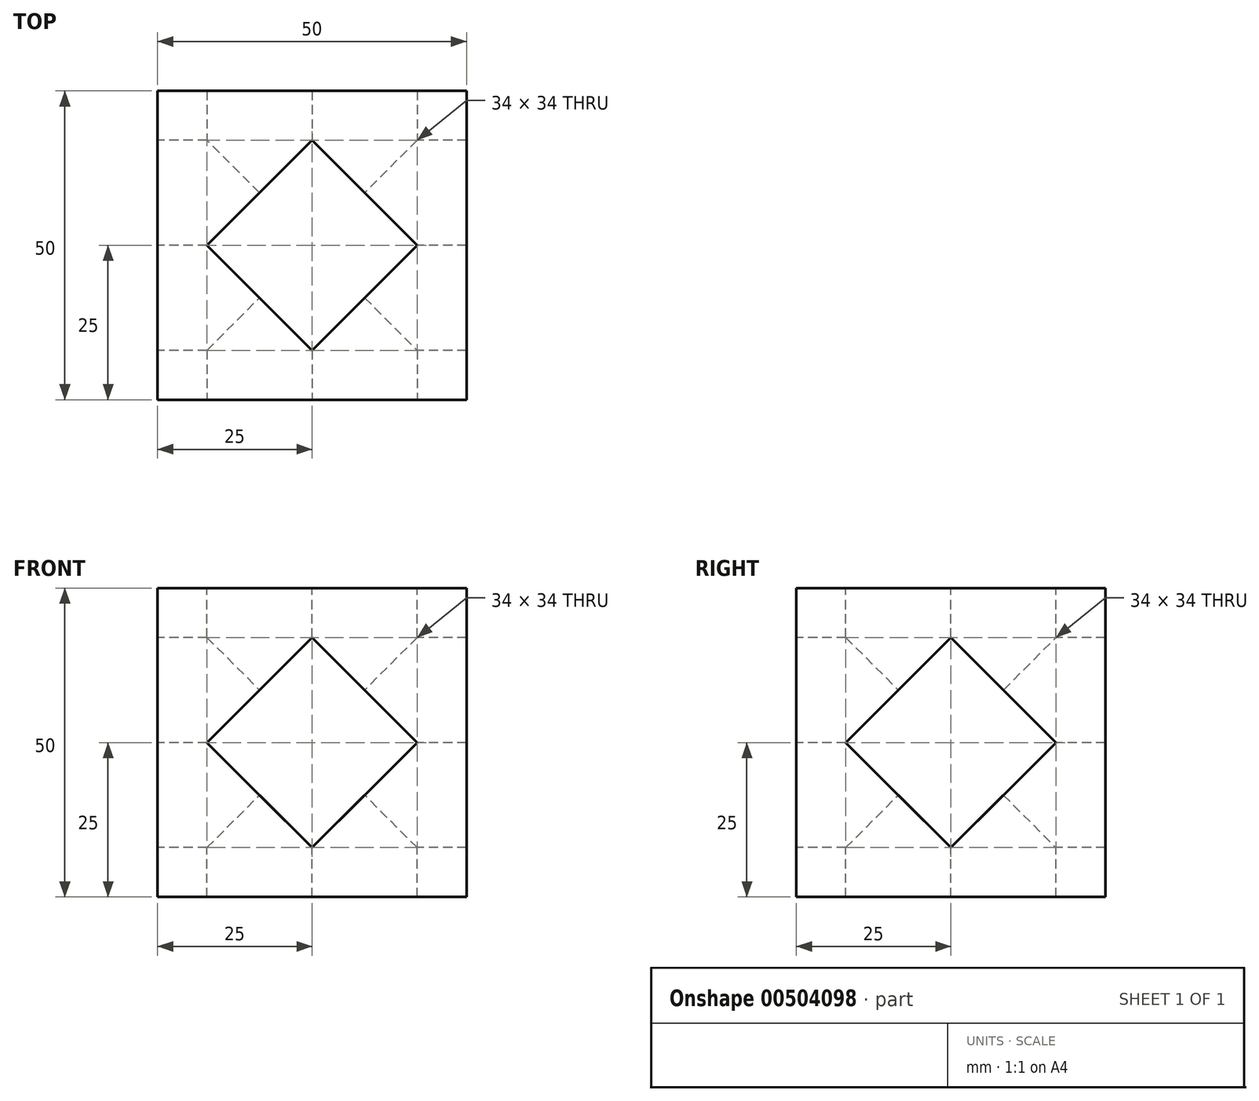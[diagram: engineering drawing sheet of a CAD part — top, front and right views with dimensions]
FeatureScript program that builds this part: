
annotation { "Feature Type Name" : "Feature", "Feature Type Description" : "" }
export const myFeature = defineFeature(function(context is Context, id is Id, definition is map)
    precondition{}
    {
        {
            var Q0;
            Q0=qCreatedBy(makeId("Top.planeOp"),FACE);
            var sketch = newSketch(context, id + "F0", { "sketchPlane" : qUnion([Q0])});
            skLineSegment(sketch, "E0.bottom", {"start": v(-25, -25) * mm, "end": v(25, -25) * mm});
            skLineSegment(sketch, "E0.top", {"start": v(-25, 25) * mm, "end": v(25, 25) * mm});
            skLineSegment(sketch, "E0.left", {"start": v(-25, -25) * mm, "end": v(-25, 25) * mm});
            skLineSegment(sketch, "E0.right", {"start": v(25, -25) * mm, "end": v(25, 25) * mm});
            skSolve(sketch);
        }
        {
            var Q0;
            Q0=makeQuery(id+"F0.imprint","IMPRINT",FACE,{"disambiguationData":[TD([[makeQuery(id+"F0.imprint","IMPRINT",EDGE,{"derivedFrom":sQuery(id+"F0.wireOp",EDGE,"E0.bottom")}),1.0]])]});
            extrude(context, id + "F1", {"entities" : qUnion([Q0]), "depth" : 50 * mm});
        }
        {
            var Q0;
            Q0=makeQuery(id+"F1.opExtrude","SWEPT_FACE",FACE,{"disambiguationData":[OSD([sQuery(id+"F0.wireOp",EDGE,"E0.bottom")])]});
            var sketch = newSketch(context, id + "F2", { "sketchPlane" : qUnion([Q0])});
            skLineSegment(sketch, "E1", {"start": v(0, 42) * mm, "end": v(17, 25) * mm});
            skLineSegment(sketch, "E2", {"start": v(17, 25) * mm, "end": v(0, 8) * mm});
            skLineSegment(sketch, "E3", {"start": v(0, 8) * mm, "end": v(-17, 25) * mm});
            skLineSegment(sketch, "E4", {"start": v(-17, 25) * mm, "end": v(0, 42) * mm});
            skSolve(sketch);
        }
        {
            var Q0;
            Q0=makeQuery(id+"F2.imprint","IMPRINT",FACE,{"disambiguationData":[TD([[makeQuery(id+"F2.imprint","IMPRINT",EDGE,{"derivedFrom":sQuery(id+"F2.wireOp",EDGE,"E1")}),-1.0]])]});
            extrude(context, id + "F3", {"entities" : qUnion([Q0]), "operationType" : NewBodyOperationType.REMOVE, "oppositeDirection" : true, "depth" : 50 * mm});
        }
        {
            var Q0;
            Q0=makeQuery(id+"F1.opExtrude","SWEPT_FACE",FACE,{"disambiguationData":[OSD([sQuery(id+"F0.wireOp",EDGE,"E0.left")])]});
            var sketch = newSketch(context, id + "F4", { "sketchPlane" : qUnion([Q0])});
            skLineSegment(sketch, "E5", {"start": v(0, 42) * mm, "end": v(17, 25) * mm});
            skLineSegment(sketch, "E6", {"start": v(17, 25) * mm, "end": v(0, 8) * mm});
            skLineSegment(sketch, "E7", {"start": v(0, 8) * mm, "end": v(-17, 25) * mm});
            skLineSegment(sketch, "E8", {"start": v(-17, 25) * mm, "end": v(0, 42) * mm});
            skSolve(sketch);
        }
        {
            var Q0;
            Q0=makeQuery(id+"F4.imprint","IMPRINT",FACE,{"disambiguationData":[TD([[makeQuery(id+"F4.imprint","IMPRINT",EDGE,{"derivedFrom":sQuery(id+"F4.wireOp",EDGE,"E5")}),-1.0]])]});
            extrude(context, id + "F5", {"entities" : qUnion([Q0]), "operationType" : NewBodyOperationType.REMOVE, "oppositeDirection" : true, "depth" : 50 * mm});
        }
        {
            var Q0;
            Q0=makeQuery(id+"F1.opExtrude","CAP_FACE",FACE,{"disambiguationData":[OSD([sQuery(id+"F0.wireOp",EDGE,"E0.bottom"),sQuery(id+"F0.wireOp",EDGE,"E0.top"),sQuery(id+"F0.wireOp",EDGE,"E0.left"),sQuery(id+"F0.wireOp",EDGE,"E0.right")])],"isStart":false});
            var sketch = newSketch(context, id + "F6", { "sketchPlane" : qUnion([Q0])});
            skLineSegment(sketch, "E9", {"start": v(0, 17) * mm, "end": v(17, 0) * mm});
            skLineSegment(sketch, "E10", {"start": v(17, 0) * mm, "end": v(0, -17) * mm});
            skLineSegment(sketch, "E11", {"start": v(0, -17) * mm, "end": v(-17, 0) * mm});
            skLineSegment(sketch, "E12", {"start": v(-17, 0) * mm, "end": v(0, 17) * mm});
            skSolve(sketch);
        }
        {
            var Q0;
            Q0=makeQuery(id+"F6.imprint","IMPRINT",FACE,{"disambiguationData":[TD([[makeQuery(id+"F6.imprint","IMPRINT",EDGE,{"derivedFrom":sQuery(id+"F6.wireOp",EDGE,"E9")}),-1.0]])]});
            extrude(context, id + "F7", {"entities" : qUnion([Q0]), "operationType" : NewBodyOperationType.REMOVE, "oppositeDirection" : true, "depth" : 50 * mm});
        }
    });
